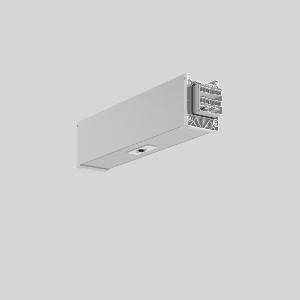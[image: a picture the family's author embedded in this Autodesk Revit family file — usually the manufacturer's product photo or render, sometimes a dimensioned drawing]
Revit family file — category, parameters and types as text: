
# Revit family: linedo_sensormodule_2-5_m_9503s1_000_700_000_cd86
name_source: partatom
category: Lighting Fixtures
units: mm (PartAtom-declared; Revit-internal decimal feet)

## family parameters
Cut with Voids When Loaded = No
Host = Face
Light Source = No
Part Type = Normal
Room Calculation Point = No
Round Connector Dimension = Use Diameter
Shared = No

## types (1)
- LINEDO Sensormodule 2-5 m
    Apparent Load = 0 VA
    Default Elevation = 1800 mm
    Description = Series: LINEDO
Module including Passive Infrared (PIR) sensor for movement and ambient light. System profile made of aluminium extrusion profile, anodised. Simple, tool-free installation of system profiles using separate accessories for cable, chain or ceiling suspension. Tool-free connection and mechanical connectors to secure. 7-poles LINEDO connector (5 x 2.5 mm² / 2 x 1.5 mm²). Phase can be set via patended bridge without opening the luminaire. Pre-assembled connector for DALI line. Light and movement sensor: Housing of non-flammable, halogen-free plastic (polycarbonate). Presence detection with passive IR element. Presence detection range adjustable via integrated shutters between 40° and 90°. Detection range: 6 m. Light sensor range: 20-800 lx (measured at the sensor). Function display with two-colour LED. Installation height: 2-5 m. Example of use: Monitoring of low ceiling rooms and rack storage where the installation height is normal. Please order supply module, connection and mounting accessories separately. 
Colour: anodised aluminium
Length: 330 mm
Width: 58 mm
Height: 76 mm
Weight: 745 g
Type of Installation: Recessed mounting
    Height = 77 mm
    Lamp = 0 x
    Length = 331 mm
    Luminous efficacy = 0 lm/W
    Manufacturer = RZB
    ModVariant = No
    Model = 9503S1.000.700.000
    Mounting Place = Ceiling
    Mounting Type = Surface mounted, Pendant
    Number of Poles = 1
    OnlyDefault = Yes
    Power Factor = 1
    Product Name = LINEDO Sensormodule 2-5 m
    Product group = Surface mounted continuous line luminaire system
    ProductGroupID = 310
    Protection Class = Protection class I
    Protection Degree = IP 20
    RLX_Detail_Level = 1
    RLX_Emergency_Light_Flux = 0 lm
    RLX_Emergency_Type = 0
    RLX_Emergency_Type_DB = No
    RlxData = <blob elided: 22745 chars, md5=8e71d7d1>
    Standby Power = 0 W
    System Light Flux = 0 lm
    System Power = 0 W
    Type Comments = Product without accessories
    Type Image = 9503s1.000.400.000.jpg
    URL = http://relux.com
    VarID = ---
    Voltage = 230 V
    Voltage Range = 220-240 V
    Weight = 0.00 kg
    Width = 58 mm

## geometry (parser evidence)
native form markers: Blend x4, Sweep x13
no freeform markers — native parametric forms only
